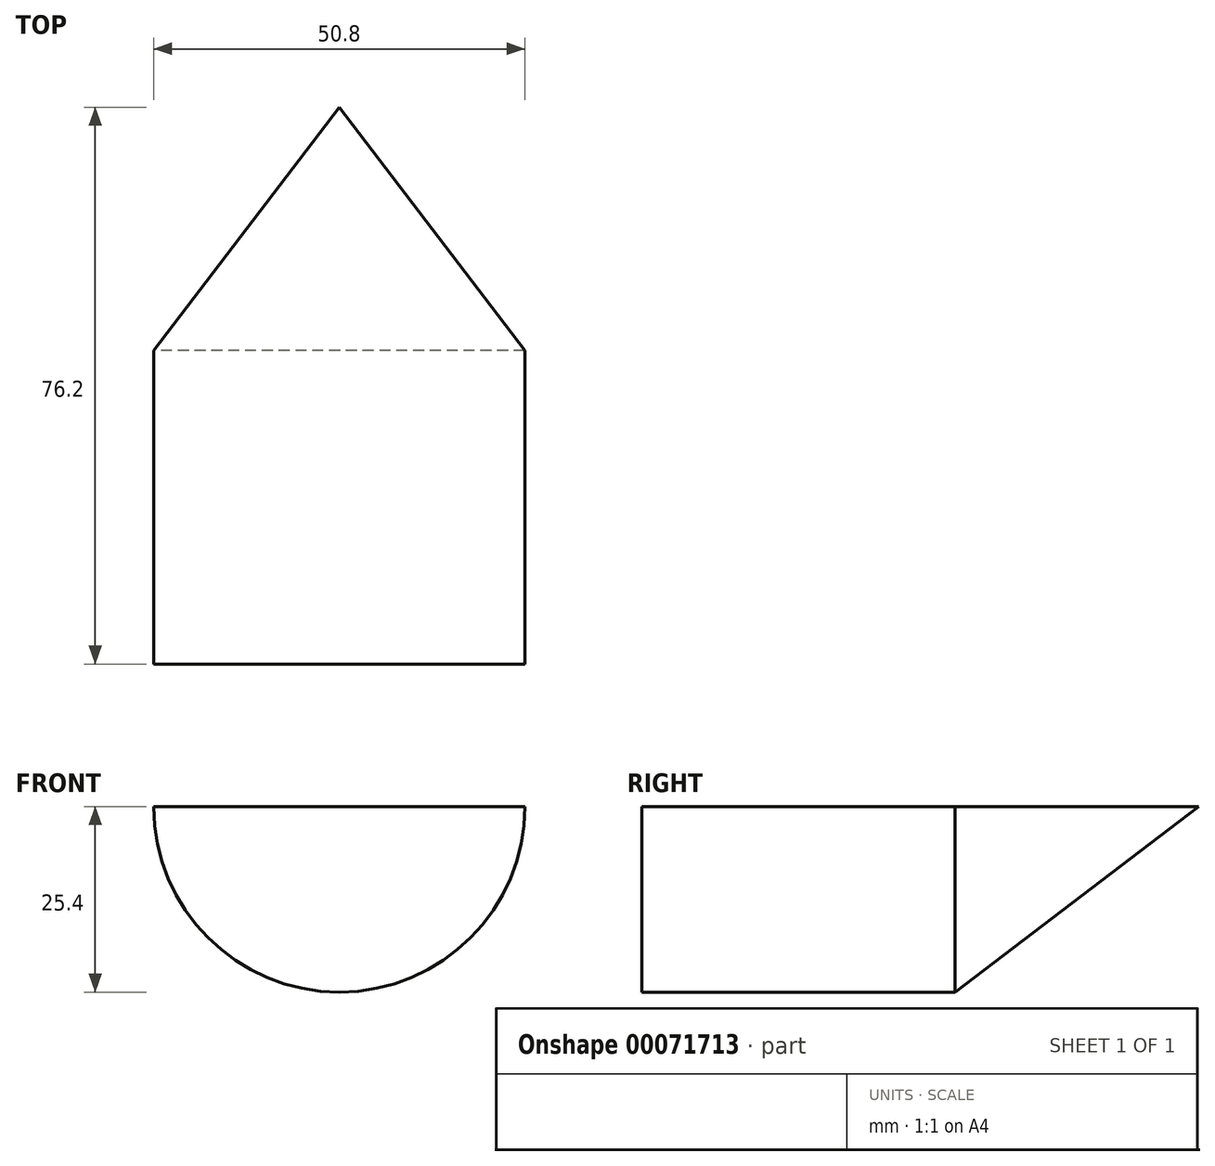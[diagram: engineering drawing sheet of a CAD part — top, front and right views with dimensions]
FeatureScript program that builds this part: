
annotation { "Feature Type Name" : "Feature", "Feature Type Description" : "" }
export const myFeature = defineFeature(function(context is Context, id is Id, definition is map)
    precondition{}
    {
        {
            var Q0;
            Q0=qCreatedBy(makeId("Top.planeOp"),FACE);
            var sketch = newSketch(context, id + "F0", { "sketchPlane" : qUnion([Q0])});
            skLineSegment(sketch, "E0", {"start": v(0, 33.32) * mm, "end": v(-25.4, 0) * mm});
            skLineSegment(sketch, "E1", {"start": v(-25.4, 0) * mm, "end": v(-25.4, -42.88) * mm});
            skLineSegment(sketch, "E2", {"start": v(-25.4, -42.88) * mm, "end": v(25.4, -42.88) * mm});
            skLineSegment(sketch, "E3", {"start": v(25.4, -42.88) * mm, "end": v(25.4, 0) * mm});
            skLineSegment(sketch, "E4", {"start": v(25.4, 0) * mm, "end": v(0, 33.32) * mm});
            skLineSegment(sketch, "E5", {"start": v(0, 33.32) * mm, "end": v(0, -42.88) * mm});
            skSolve(sketch);
        }
        {
            var Q0;
            Q0=makeQuery(id+"F0.imprint","IMPRINT",FACE,{"disambiguationData":[TD([[makeQuery(id+"F0.imprint","IMPRINT",EDGE,{"derivedFrom":sQuery(id+"F0.wireOp",EDGE,"E0")}),1.0]])]});
            var Q1;
            Q1=sQuery(id+"F0.wireOp",EDGE,"E5");
            revolve(context, id + "F1", {"entities" : qUnion([Q0]), "axis" : qUnion([Q1]), "revolveType" : RevolveType.ONE_DIRECTION, "angle" : 180 * degree});
        }
    });
